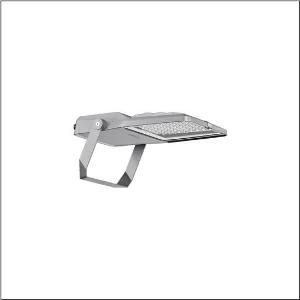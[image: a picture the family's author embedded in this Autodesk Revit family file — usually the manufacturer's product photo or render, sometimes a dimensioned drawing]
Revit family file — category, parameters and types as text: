
# Revit family: floodlight_fl_21_iq_mini___rs12_5xa7771b4b1a_1748
name_source: partatom
category: Lighting Fixtures
units: mm (PartAtom-declared; Revit-internal decimal feet)

## family parameters
Cut with Voids When Loaded = No
Host = Face
Light Source = No
Part Type = Normal
Room Calculation Point = No
Round Connector Dimension = Use Diameter
Shared = No

## types (1)
- --- (1 x LED, 6560 lm, 45.5 W, 4000K)
    Apparent Load = 46 VA
    CIE Flux Codes = 79 92 99 100 100
    Color Rendering = 70
    Color Temperature = 4000K
    Default Elevation = 1800 mm
    Description = Floodlight FL 21 iQ mini, floodlight, primary light control with lens, of PMMA, primary optical cover: protective disc, of toughened safety glass, transparent, light distribution: RS12, light emission: direct distribution, installation type: surface-mounted, LED, High Power LED, rated luminous flux: 6.560lm, luminous efficacy: 144lm/W, light colour: 740, colour temperature: 4000K, control: Auto-Match, Temp-Guard, Lumen-Switch, Night-Set, Smart-Wire, Light-Fading, Desk-Remote (wireless, voltage-free reading and setting of iQ features in the workshop via application-optimized NFC function/RFID function), optimised constant luminous flux control (CLO 2.0), with terminal, 6-pole, mains connection: 220..240V, AC, 50/60Hz, start of lifetime: 46W, end of service life: 48W, reduction: 22W, luminaire housing, of diecast aluminium, powder-coated, Siteco® metallic grey (DB 702S), corrosivity category C5 mid according to DIN EN ISO 12944, sealing non-destructively replaceable, mounting bracket, of steel, galvanised, powder-coated, Siteco® metallic grey (DB 702S), protection rating (complete): IP66, insulation class (complete): insulation class II (safety insulation), certification: CE, ENEC, VDE, protection symbol: D, impact resistance: IK08, permissible operating ambient temperature: -40..+40°C, permissible operating ambient temperature for outdoor applications: -40..+50°C, standard: DIN EN 12944, LABS conformity tested according to VDMA 24364:2018-05, packaging unit: 1 piece

Light Distribution: RS12
    Height = 70 mm
    Lamp = 1 x LED
    Lamp Light Flux = 6560 lm
    Lamp Power = 45.5 W
    Lamp count = 1
    Length = 485 mm
    Luminous efficacy = 144 lm/W
    Manufacturer = Siteco
    ModVariant = No
    Model = 5XA7771B4B1A
    Mounting Place = Wall
    Mounting Type = Surface mounted
    Number of Poles = 1
    OnlyDefault = Yes
    Power Factor = 1
    Product Name = Floodlight FL 21 iQ mini | RS12
    Product group = floodlight | wall mounted
    ProductGroupID = 2001
    Protection Class = Protection class II
    Protection Degree = IP 66
    RLX_Detail_Level = 1
    RLX_Emergency_Light_Flux = 0 lm
    RLX_Emergency_Type = 0
    RLX_Emergency_Type_DB = No
    RlxData = <blob elided: 90873 chars, md5=0c831279>
    Socket = socket
    Standby Power = 0 W
    System Light Flux = 6560 lm
    System Power = 46 W
    Type Comments = factory setting: luminous flux: 100 % | dim-lin: 254 | 463 mA
    Type Image = l_1006845.jpg
    URL = http://relux.com
    VarID = @adj_100275
    Voltage = 0 V
    Weight = 0.00 kg
    Width = 337 mm

## geometry (parser evidence)
native form markers: Blend x4, Sweep x15
no freeform markers — native parametric forms only
